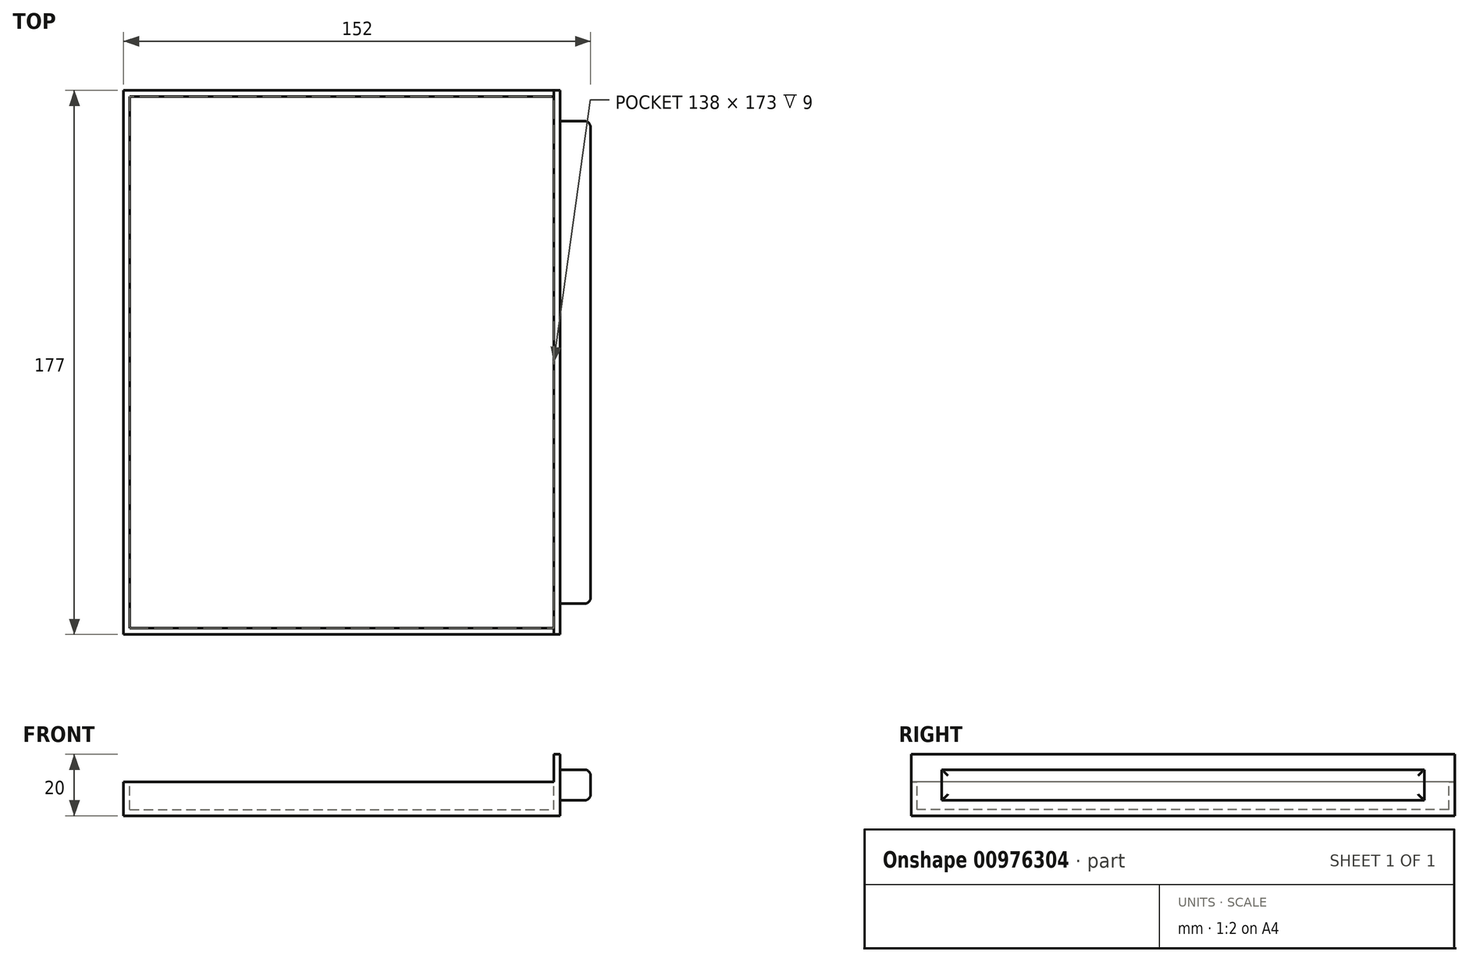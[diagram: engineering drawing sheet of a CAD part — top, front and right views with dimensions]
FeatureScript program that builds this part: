
annotation { "Feature Type Name" : "Feature", "Feature Type Description" : "" }
export const myFeature = defineFeature(function(context is Context, id is Id, definition is map)
    precondition{}
    {
        {
            var Q0;
            Q0=qCreatedBy(makeId("Top.planeOp"),FACE);
            var sketch = newSketch(context, id + "F0", { "sketchPlane" : qUnion([Q0])});
            skLineSegment(sketch, "E0.bottom", {"start": v(-60.91, 103.97) * mm, "end": v(81.09, 103.97) * mm});
            skLineSegment(sketch, "E0.top", {"start": v(-60.91, -73.03) * mm, "end": v(81.09, -73.03) * mm});
            skLineSegment(sketch, "E0.left", {"start": v(-60.91, 103.97) * mm, "end": v(-60.91, -73.03) * mm});
            skLineSegment(sketch, "E0.right", {"start": v(81.09, 103.97) * mm, "end": v(81.09, -73.03) * mm});
            skSolve(sketch);
        }
        {
            var Q0;
            Q0=makeQuery(id+"F0.imprint","IMPRINT",FACE,{"disambiguationData":[TD([[makeQuery(id+"F0.imprint","IMPRINT",EDGE,{"derivedFrom":sQuery(id+"F0.wireOp",EDGE,"E0.bottom")}),-1.0]])]});
            extrude(context, id + "F1", {"entities" : qUnion([Q0]), "depth" : 20 * mm, "offsetDistance" : 25 * mm});
        }
        {
            var Q0;
            Q0=makeQuery(id+"F1.opExtrude","CAP_FACE",FACE,{"disambiguationData":[OSD([sQuery(id+"F0.wireOp",EDGE,"E0.bottom"),sQuery(id+"F0.wireOp",EDGE,"E0.top"),sQuery(id+"F0.wireOp",EDGE,"E0.left"),sQuery(id+"F0.wireOp",EDGE,"E0.right")])],"isStart":false});
            var sketch = newSketch(context, id + "F2", { "sketchPlane" : qUnion([Q0])});
            skLineSegment(sketch, "E1", {"start": v(79.09, -73.03) * mm, "end": v(79.09, 103.97) * mm});
            skLineSegment(sketch, "E2", {"start": v(79.09, 101.97) * mm, "end": v(-58.91, 101.97) * mm});
            skLineSegment(sketch, "E3", {"start": v(-58.91, 101.97) * mm, "end": v(-58.91, -71.03) * mm});
            skLineSegment(sketch, "E4", {"start": v(-58.91, -71.03) * mm, "end": v(79.09, -71.03) * mm});
            skSolve(sketch);
        }
        {
            var Q0;
            {var subQ0=sQuery(id+"F2.wireOp",EDGE,"E2");Q0=makeQuery(id+"F2.imprint","IMPRINT",FACE,{"disambiguationData":[TD([[makeQuery(id+"F2.imprint","IMPRINT",EDGE,{"derivedFrom":subQ0}),1.0]])]});}
            extrude(context, id + "F3", {"entities" : qUnion([Q0]), "operationType" : NewBodyOperationType.REMOVE, "oppositeDirection" : true, "depth" : 18 * mm, "offsetDistance" : 25 * mm});
        }
        {
            var Q0;
            {var subQ0=sQuery(id+"F2.wireOp",EDGE,"E2");Q0=makeQuery(id+"F2.imprint","IMPRINT",FACE,{"disambiguationData":[TD([[makeQuery(id+"F2.imprint","IMPRINT",EDGE,{"derivedFrom":subQ0}),-1.0]])]});}
            extrude(context, id + "F4", {"entities" : qUnion([Q0]), "operationType" : NewBodyOperationType.REMOVE, "oppositeDirection" : true, "depth" : 9 * mm, "offsetDistance" : 25 * mm});
        }
        {
            var Q0;
            Q0=makeQuery(id+"F1.opExtrude","SWEPT_FACE",FACE,{"disambiguationData":[OSD([sQuery(id+"F0.wireOp",EDGE,"E0.right")])]});
            var sketch = newSketch(context, id + "F5", { "sketchPlane" : qUnion([Q0])});
            skLineSegment(sketch, "E5.bottom", {"start": v(-63.03, 15) * mm, "end": v(93.97, 15) * mm});
            skLineSegment(sketch, "E5.top", {"start": v(-63.03, 5) * mm, "end": v(93.97, 5) * mm});
            skLineSegment(sketch, "E5.left", {"start": v(-63.03, 15) * mm, "end": v(-63.03, 5) * mm});
            skLineSegment(sketch, "E5.right", {"start": v(93.97, 15) * mm, "end": v(93.97, 5) * mm});
            skSolve(sketch);
        }
        {
            var Q0;
            Q0=makeQuery(id+"F5.imprint","IMPRINT",FACE,{"disambiguationData":[TD([[makeQuery(id+"F5.imprint","IMPRINT",EDGE,{"derivedFrom":sQuery(id+"F5.wireOp",EDGE,"E5.bottom")}),-1.0]])]});
            extrude(context, id + "F6", {"entities" : qUnion([Q0]), "operationType" : NewBodyOperationType.ADD, "depth" : 10 * mm, "offsetDistance" : 25 * mm});
        }
        {
            var Q0;
            Q0=makeQuery(id+"F6.opExtrude","CAP_EDGE",EDGE,{"disambiguationData":[OSD([sQuery(id+"F5.wireOp",EDGE,"E5.bottom")])],"isStart":false});
            var Q1;
            Q1=makeQuery(id+"F6.opExtrude","CAP_EDGE",EDGE,{"disambiguationData":[OSD([sQuery(id+"F5.wireOp",EDGE,"E5.top")])],"isStart":false});
            var Q2;
            Q2=makeQuery(id+"F6.opExtrude","CAP_EDGE",EDGE,{"disambiguationData":[OSD([sQuery(id+"F5.wireOp",EDGE,"E5.left")])],"isStart":false});
            var Q3;
            Q3=makeQuery(id+"F6.opExtrude","CAP_EDGE",EDGE,{"disambiguationData":[OSD([sQuery(id+"F5.wireOp",EDGE,"E5.right")])],"isStart":false});
            fillet(context, id + "F7", {"entities" : qUnion([Q0, Q1, Q2, Q3]), "radius" : 2 * mm, "tangentPropagation" : true, "allowEdgeOverflow" : false});
        }
    });
